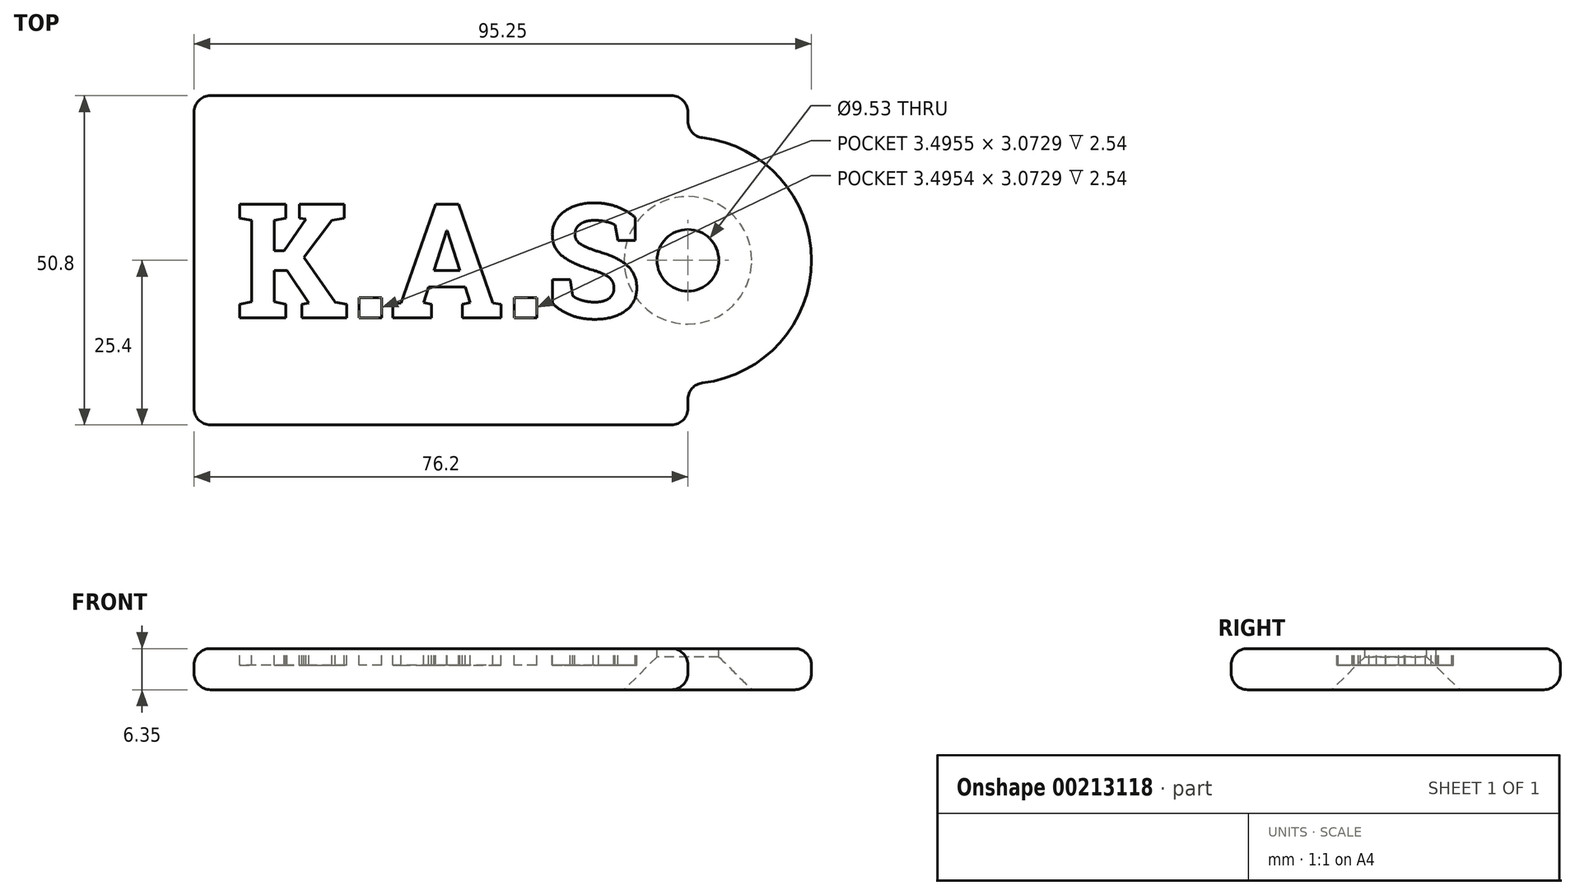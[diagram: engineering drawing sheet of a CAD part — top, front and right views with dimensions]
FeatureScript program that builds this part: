
annotation { "Feature Type Name" : "Feature", "Feature Type Description" : "" }
export const myFeature = defineFeature(function(context is Context, id is Id, definition is map)
    precondition{}
    {
        {
            var Q0;
            Q0=qCreatedBy(makeId("Top.planeOp"),FACE);
            var sketch = newSketch(context, id + "F0", { "sketchPlane" : qUnion([Q0])});
            skLineSegment(sketch, "E0.bottom", {"start": v(0, 0) * mm, "end": v(76.2, 0) * mm});
            skLineSegment(sketch, "E0.top", {"start": v(0, 50.8) * mm, "end": v(76.2, 50.8) * mm});
            skLineSegment(sketch, "E0.left", {"start": v(0, 0) * mm, "end": v(0, 50.8) * mm});
            skLineSegment(sketch, "E0.right", {"start": v(76.2, 0) * mm, "end": v(76.2, 50.8) * mm});
            skSolve(sketch);
        }
        {
            var Q0;
            Q0=makeQuery(id+"F0.imprint","IMPRINT",FACE,{"disambiguationData":[TD([[makeQuery(id+"F0.imprint","IMPRINT",EDGE,{"derivedFrom":sQuery(id+"F0.wireOp",EDGE,"E0.bottom")}),1.0]])]});
            extrude(context, id + "F1", {"entities" : qUnion([Q0]), "depth" : 6.35 * mm});
        }
        {
            var Q0;
            Q0=makeQuery(id+"F1.opExtrude","CAP_FACE",FACE,{"disambiguationData":[OSD([sQuery(id+"F0.wireOp",EDGE,"E0.bottom"),sQuery(id+"F0.wireOp",EDGE,"E0.top"),sQuery(id+"F0.wireOp",EDGE,"E0.left"),sQuery(id+"F0.wireOp",EDGE,"E0.right")])],"isStart":false});
            var sketch = newSketch(context, id + "F2", { "sketchPlane" : qUnion([Q0])});
            skCircle(sketch, "E1", {"center": v(76.2, 25.4) * mm, "radius": 19.05 * mm});
            skSolve(sketch);
        }
        {
            var Q0;
            {var subQ0=sQuery(id+"F2.wireOp",EDGE,"E1");var subQ1=makeQuery(id+"F1.opExtrude","CAP_EDGE",EDGE,{"disambiguationData":[OSD([sQuery(id+"F0.wireOp",EDGE,"E0.right")])],"isStart":false});var subQ2=makeQuery(id+"F2.imprint","INTERSECT",VERTEX,{"disambiguationData":[OD(0.0)],"derivedFrom":[subQ1,subQ0]});Q0=makeQuery(id+"F2.imprint","IMPRINT",FACE,{"disambiguationData":[TD([[makeQuery(id+"F2.imprint","IMPRINT",EDGE,{"disambiguationData":[TD([[subQ2,-1.0]])],"derivedFrom":subQ0}),1.0]])]});}
            var Q1;
            Q1 = qSketchRegion(id + "F4", true);
            var Q2;
            Q2=sQuery(id+"F2.wireOp",EDGE,"E1");
            extrude(context, id + "F3", {"entities" : qUnion([Q0, Q1]), "operationType" : NewBodyOperationType.ADD, "surfaceEntities" : qUnion([Q2]), "oppositeDirection" : true, "depth" : 6.35 * mm});
        }
        {
            var Q0;
            {var subQ0=sQuery(id+"F0.wireOp",EDGE,"E0.right");Q0=makeQuery(id+"F3.boolean.opBoolean","MERGE",FACE,{"derivedFrom":[makeQuery(id+"F1.opExtrude","CAP_FACE",FACE,{"disambiguationData":[OSD([sQuery(id+"F0.wireOp",EDGE,"E0.bottom"),sQuery(id+"F0.wireOp",EDGE,"E0.top"),sQuery(id+"F0.wireOp",EDGE,"E0.left"),subQ0])],"isStart":false}),makeQuery(id+"F3.opExtrude","CAP_FACE",FACE,{"disambiguationData":[OSD([subQ0,sQuery(id+"F2.wireOp",EDGE,"E1")])],"isStart":true})]});}
            var sketch = newSketch(context, id + "F4", { "sketchPlane" : qUnion([Q0])});
            skText(sketch, "E2", { "text": "K.A.S", "fontName": "RobotoSlab-Bold.ttf"});
            skLineSegment(sketch, "E3", {"start": v(0, 25.4) * mm, "end": v(6.35, 25.4) * mm, "construction": true});
            const initialGuessF4  = {"E2": [0.00635, 0.01655, 1, 0, 0.0177]};
            skSetInitialGuess(sketch, initialGuessF4);
            skSolve(sketch);
        }
        {
            var Q0;
            Q0 = qSketchRegion(id + "F4", true);
            var Q1;
            Q1 = qSketchRegion(id + "F6", true);
            var Q2;
            Q2 = qConstructionFilter(qBodyType(qCreatedBy(id + "F4" ,EDGE), BodyType.WIRE), ConstructionObject.NO);
            extrude(context, id + "F5", {"entities" : qUnion([Q0, Q1]), "operationType" : NewBodyOperationType.REMOVE, "surfaceEntities" : qUnion([Q2]), "oppositeDirection" : true, "depth" : 2.54 * mm});
        }
        {
            var Q0;
            {var subQ0=sQuery(id+"F2.wireOp",EDGE,"E1");var subQ1=sQuery(id+"F0.wireOp",EDGE,"E0.bottom");var subQ2=sQuery(id+"F0.wireOp",EDGE,"E0.right");var subQ3=sQuery(id+"F0.wireOp",EDGE,"E0.top");var subQ4=sQuery(id+"F0.wireOp",EDGE,"E0.left");Q0=makeQuery(id+"F5.boolean.opBoolean","SPLIT",FACE,{"disambiguationData":[TD([makeQuery(id+"F1.opExtrude","SWEPT_FACE",FACE,{"disambiguationData":[OSD([subQ1])]})])],"derivedFrom":makeQuery(id+"F3.boolean.opBoolean","MERGE",FACE,{"derivedFrom":[makeQuery(id+"F1.opExtrude","CAP_FACE",FACE,{"disambiguationData":[OSD([subQ1,subQ3,subQ4,subQ2])],"isStart":false}),makeQuery(id+"F3.opExtrude","CAP_FACE",FACE,{"disambiguationData":[OSD([subQ2,subQ0])],"isStart":true})]})});}
            var sketch = newSketch(context, id + "F6", { "sketchPlane" : qUnion([Q0])});
            skCircle(sketch, "E4", {"center": v(76.2, 25.4) * mm, "radius": 4.76 * mm});
            skLineSegment(sketch, "E5", {"start": v(76.2, 6.35) * mm, "end": v(76.2, 44.45) * mm, "construction": true});
            skLineSegment(sketch, "E6", {"start": v(95.25, 25.4) * mm, "end": v(76.2, 25.4) * mm, "construction": true});
            skSolve(sketch);
        }
        {
            var Q0;
            Q0=makeQuery(id+"F6.imprint","IMPRINT",FACE,{"disambiguationData":[TD([[makeQuery(id+"F6.imprint","IMPRINT",EDGE,{"derivedFrom":sQuery(id+"F6.wireOp",EDGE,"E4")}),1.0]])]});
            extrude(context, id + "F7", {"entities" : qUnion([Q0]), "operationType" : NewBodyOperationType.REMOVE, "endBound" : BoundingType.THROUGH_ALL, "oppositeDirection" : true, "depth" : mm});
        }
        {
            var Q0;
            Q0=makeQuery(id+"F1.opExtrude","CAP_EDGE",EDGE,{"disambiguationData":[OSD([sQuery(id+"F0.wireOp",EDGE,"E0.top")])],"isStart":false});
            var Q1;
            Q1=makeQuery(id+"F1.opExtrude","CAP_EDGE",EDGE,{"disambiguationData":[OSD([sQuery(id+"F0.wireOp",EDGE,"E0.left")])],"isStart":false});
            var Q2;
            Q2=makeQuery(id+"F1.opExtrude","CAP_EDGE",EDGE,{"disambiguationData":[OSD([sQuery(id+"F0.wireOp",EDGE,"E0.bottom")])],"isStart":true});
            var Q3;
            Q3=makeQuery(id+"F1.opExtrude","CAP_EDGE",EDGE,{"disambiguationData":[OSD([sQuery(id+"F0.wireOp",EDGE,"E0.bottom")])],"isStart":false});
            var Q4;
            Q4=makeQuery(id+"F3.opExtrude","CAP_EDGE",EDGE,{"disambiguationData":[OSD([sQuery(id+"F2.wireOp",EDGE,"E1")])],"isStart":true});
            var Q5;
            Q5=makeQuery(id+"F3.opExtrude","CAP_EDGE",EDGE,{"disambiguationData":[OSD([sQuery(id+"F2.wireOp",EDGE,"E1")])],"isStart":false});
            var Q6;
            {var subQ0=sQuery(id+"F0.wireOp",EDGE,"E0.top");var subQ1=sQuery(id+"F0.wireOp",EDGE,"E0.right");Q6=makeQuery(id+"F3.boolean.opBoolean","SPLIT",FACE,{"disambiguationData":[TD([makeQuery(id+"F1.opExtrude","SWEPT_FACE",FACE,{"disambiguationData":[OSD([subQ0])]})])],"derivedFrom":makeQuery(id+"F1.opExtrude","SWEPT_FACE",FACE,{"disambiguationData":[OSD([subQ1])]})});}
            var Q7;
            {var subQ0=sQuery(id+"F0.wireOp",EDGE,"E0.right");var subQ3=sQuery(id+"F0.wireOp",EDGE,"E0.bottom");Q7=makeQuery(id+"F3.boolean.opBoolean","SPLIT",FACE,{"disambiguationData":[TD([makeQuery(id+"F1.opExtrude","SWEPT_FACE",FACE,{"disambiguationData":[OSD([subQ3])]})])],"derivedFrom":makeQuery(id+"F1.opExtrude","SWEPT_FACE",FACE,{"disambiguationData":[OSD([subQ0])]})});}
            var Q8;
            {var subQ1=sQuery(id+"F0.wireOp",EDGE,"E0.right");var subQ2=sQuery(id+"F0.wireOp",EDGE,"E0.top");Q8=makeQuery(id+"F3.boolean.opBoolean","SPLIT",EDGE,{"disambiguationData":[TD([makeQuery(id+"F1.opExtrude","SWEPT_FACE",FACE,{"disambiguationData":[OSD([subQ2])]})])],"derivedFrom":makeQuery(id+"F1.opExtrude","CAP_EDGE",EDGE,{"disambiguationData":[OSD([subQ1])],"isStart":false})});}
            var Q9;
            Q9=makeQuery(id+"F1.opExtrude","CAP_EDGE",EDGE,{"disambiguationData":[OSD([sQuery(id+"F0.wireOp",EDGE,"E0.left")])],"isStart":true});
            var Q10;
            Q10=makeQuery(id+"F1.opExtrude","SWEPT_FACE",FACE,{"disambiguationData":[OSD([sQuery(id+"F0.wireOp",EDGE,"E0.top")])]});
            var Q11;
            Q11=makeQuery(id+"F1.opExtrude","SWEPT_EDGE",EDGE,{"disambiguationData":[OSD([sQuery(id+"F0.wireOp",EDGE,"E0.bottom"),sQuery(id+"F0.wireOp",EDGE,"E0.left")])]});
            fillet(context, id + "F8", {"entities" : qUnion([Q0, Q1, Q2, Q3, Q4, Q5, Q6, Q7, Q8, Q9, Q10, Q11]), "radius" : 2.54 * mm, "tangentPropagation" : true, "allowEdgeOverflow" : false});
        }
        {
            var Q0;
            {var subQ0=sQuery(id+"F0.wireOp",EDGE,"E0.right");Q0=makeQuery(id+"F7.boolean.opBoolean","INTERSECT",EDGE,{"derivedFrom":[makeQuery(id+"F3.boolean.opBoolean","MERGE",FACE,{"derivedFrom":[makeQuery(id+"F1.opExtrude","CAP_FACE",FACE,{"disambiguationData":[OSD([sQuery(id+"F0.wireOp",EDGE,"E0.bottom"),sQuery(id+"F0.wireOp",EDGE,"E0.top"),sQuery(id+"F0.wireOp",EDGE,"E0.left"),subQ0])],"isStart":true}),makeQuery(id+"F3.opExtrude","CAP_FACE",FACE,{"disambiguationData":[OSD([subQ0,sQuery(id+"F2.wireOp",EDGE,"E1")])],"isStart":false})]}),makeQuery(id+"F7.opExtrude","SWEPT_FACE",FACE,{"disambiguationData":[OSD([sQuery(id+"F6.wireOp",EDGE,"E4")])]})]});}
            chamfer(context, id + "F9", {"entities" : qUnion([Q0]), "width" : 5.08 * mm, "tangentPropagation" : true});
        }
    });
